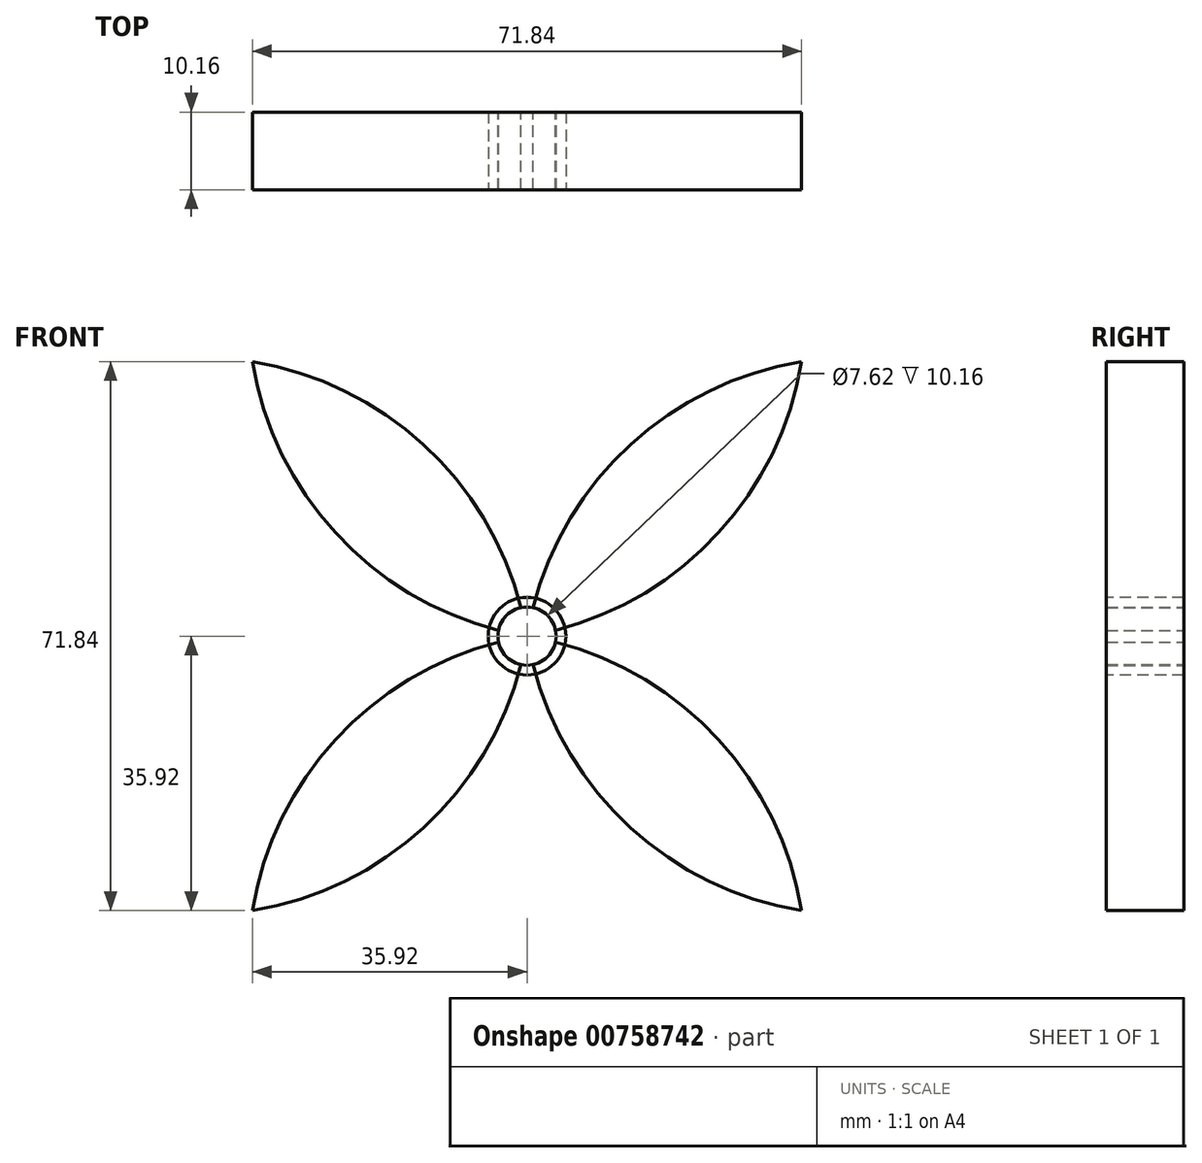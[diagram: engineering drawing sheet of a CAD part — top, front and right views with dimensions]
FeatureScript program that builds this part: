
annotation { "Feature Type Name" : "Feature", "Feature Type Description" : "" }
export const myFeature = defineFeature(function(context is Context, id is Id, definition is map)
    precondition{}
    {
        {
            var Q0;
            Q0=qCreatedBy(makeId("Front.planeOp"),FACE);
            var sketch = newSketch(context, id + "F0", { "sketchPlane" : qUnion([Q0])});
            skCircle(sketch, "E0", {"center": v(0, 0) * mm, "radius": 50.8 * mm});
            skArc(sketch, "E1", {"start": v(35.92, 35.92) * mm, "mid": v(12.16, 23.76) * mm, "end": v(0, 0) * mm});
            skArc(sketch, "E2", {"start": v(0, 0) * mm, "mid": v(23.76, 12.16) * mm, "end": v(35.92, 35.92) * mm});
            skArc(sketch, "E3", {"start": v(-35.92, -35.92) * mm, "mid": v(-12.16, -23.76) * mm, "end": v(0, 0) * mm});
            skArc(sketch, "E4", {"start": v(0, 0) * mm, "mid": v(-23.76, -12.16) * mm, "end": v(-35.92, -35.92) * mm});
            skArc(sketch, "E5", {"start": v(-35.92, 35.92) * mm, "mid": v(-23.76, 12.16) * mm, "end": v(0, 0) * mm});
            skArc(sketch, "E6", {"start": v(0, 0) * mm, "mid": v(-12.16, 23.76) * mm, "end": v(-35.92, 35.92) * mm});
            skArc(sketch, "E7", {"start": v(0, 0) * mm, "mid": v(12.16, -23.76) * mm, "end": v(35.92, -35.92) * mm});
            skArc(sketch, "E8", {"start": v(35.92, -35.92) * mm, "mid": v(23.76, -12.16) * mm, "end": v(0, 0) * mm});
            skSolve(sketch);
        }
        {
            var Q0;
            Q0=makeQuery(id+"F0.imprint","IMPRINT",FACE,{"disambiguationData":[TD([[makeQuery(id+"F0.imprint","IMPRINT",EDGE,{"derivedFrom":sQuery(id+"F0.wireOp",EDGE,"E1")}),1.0]])]});
            var Q1;
            Q1=makeQuery(id+"F0.imprint","IMPRINT",FACE,{"disambiguationData":[TD([[makeQuery(id+"F0.imprint","IMPRINT",EDGE,{"derivedFrom":sQuery(id+"F0.wireOp",EDGE,"E3")}),1.0]])]});
            var Q2;
            Q2=makeQuery(id+"F0.imprint","IMPRINT",FACE,{"disambiguationData":[TD([[makeQuery(id+"F0.imprint","IMPRINT",EDGE,{"derivedFrom":sQuery(id+"F0.wireOp",EDGE,"E5")}),1.0]])]});
            var Q3;
            Q3=makeQuery(id+"F0.imprint","IMPRINT",FACE,{"disambiguationData":[TD([[makeQuery(id+"F0.imprint","IMPRINT",EDGE,{"derivedFrom":sQuery(id+"F0.wireOp",EDGE,"E7")}),1.0]])]});
            extrude(context, id + "F1", {"entities" : qUnion([Q0, Q1, Q2, Q3]), "depth" : 10.16 * mm, "offsetDistance" : 25.4 * mm});
        }
        {
            var Q0;
            Q0=makeQuery(id+"F1.opExtrude","CAP_FACE",FACE,{"disambiguationData":[OSD([sQuery(id+"F0.wireOp",EDGE,"E5"),sQuery(id+"F0.wireOp",EDGE,"E6")])],"isStart":false});
            var sketch = newSketch(context, id + "F2", { "sketchPlane" : qUnion([Q0])});
            skCircle(sketch, "E9", {"center": v(0, 0) * mm, "radius": 5.08 * mm});
            skSolve(sketch);
        }
        {
            var Q0;
            Q0 = qSketchRegion(id + "F2", true);
            extrude(context, id + "F3", {"entities" : qUnion([Q0]), "oppositeDirection" : true, "depth" : 10.16 * mm, "offsetDistance" : 25.4 * mm});
        }
        {
            var Q0;
            Q0=makeQuery(id+"F1.opExtrude","CAP_FACE",FACE,{"disambiguationData":[OSD([sQuery(id+"F0.wireOp",EDGE,"E3"),sQuery(id+"F0.wireOp",EDGE,"E4")])],"isStart":true});
            var sketch = newSketch(context, id + "F4", { "sketchPlane" : qUnion([Q0])});
            skCircle(sketch, "E10", {"center": v(0, 0) * mm, "radius": 3.81 * mm});
            skSolve(sketch);
        }
        {
            var Q0;
            Q0 = qSketchRegion(id + "F4", true);
            extrude(context, id + "F5", {"entities" : qUnion([Q0]), "operationType" : NewBodyOperationType.REMOVE, "oppositeDirection" : true, "depth" : 37.34 * mm, "offsetDistance" : 25.4 * mm});
        }
    });
